# Revit family: ON5DMXA-NRG
name_source: partatom
category: Mechanical Equipment
units: mm (PartAtom-declared; Revit-internal decimal feet)

## family parameters
Always vertical = Yes
Cut with Voids When Loaded = No
OmniClass Number = 23.40.40.11.17
OmniClass Title = Refrigerated Cases
Part Type = Normal
Room Calculation Point = No
Round Connector Dimension = Use Radius
Shared = No
Work Plane-Based = Yes

## types (2) — shared parameters
16" Shelf = Yes
18" Shelf = Yes
BOTTOM ELECTRICAL = Yes
BOTTOM REFRIGERATION PIPING = Yes
Certifications = NSF 7, UL471, CSA
DATE = 03/14/2017
DESIGNERS NAME = SHIDDRAMESH
DRAIN LINE = 48"
DRAIN PIPING = Yes
Default Elevation = 48"
Defrosts Per Day = 6
Description = Narrow Self-Contained Multi-Deck Merchandiser
Discharge Air (°F) = 31 °F
Discharge Air Velocity (FPM) = 200 FPM
Drain Pump Amps = 1 A
Drain Pump Watts = 47 W
EQUIPMENT DESCRIPTION = Narrow Self-Contained Multi-Deck Merchandiser
EQUIPMENT MARK = ON5DMXA-NRG
Evaporator (°F) = 0 °F
Evaporator Pan Heater  Amps = 7 A
Evaporator Pan Heater  Watts = 1500 W
Frequency (Hz) = 60 Hz
GLASS = Glass
Height = 81 1/2"
High Efficiency Amps = 0 A
High Efficiency Fan Amps = 0 A
High Efficiency Fan Watts = 28 W
High Efficiency Watts = 28 W
High Power (Cornice) Amps = 0 A
High Power (Cornice) Watts = 0 W
Item Description = Narrow Self-Contained Multi-Deck Merchandiser
LF STD END = Yes
Legend Number = ON5DMXA-NRG
Light Length = 0
Manufacturer = HILL PHOENIX
Maximum Lights Amps = 1 A
Maximum Overcurrent Protection = 35 A
Minimum Circuit Ampacity = 25 A
Model = ON5DMXA-NRG
Number of Fans = 2
PAINTED METAL UPPER SHELF = PAINTED SHELVES
PHASE = 1
REAR REFRIGERATION PIPING = Yes
REF = 28 5/8"
REFRIGERATION PIPING = COPPER PIPE
RT STD END = Yes
Refgn = 8 3/4"
Refrigerant = R404A
STAINLESS STEEL = GALVANIZED STEEL
Standard Power Amps = 0 A
Standard Power Watts = 0 W
Suction Pressure @ Case Outlet (psig) = 58
TOP ELECTRICAL = Yes
TOP REFRIGERATION PIPING = Yes
Timed-Off Defrost Fail-Safe (Min) = 42 (Min)
Timed-Off Defrost Termination Temp = 42 °F
URL = http://www.hillphoenix.com
Volts = 208 V
Width = 35 3/4"
Wire = 3 wire + ground
zero-valued in all types: BTUH Conventional, BTUH Parallel, Lights Per Row

## per-type parameters (varying)
| type | CENTER LINE | Horsepower | Lbs. Of Refrigerant | Length | Length of Cases | Locked Rotor Amps (LRA) (Amps) | Maximum Lights Watts | Running Load Amps (RLA) (Amps) | Timed-Off Defrost Fail Safe (Min) |
| 08' | 48" | 2 | 5.60 | 96" | 96" | 56 A | 144 W | 12 A | -460 °F |
| 06' | 36" | 1-3/4 | 5 | 72" | 72" | 55 A | 100 W | 13 A | 45 °F |

## geometry (parser evidence)
native form markers: Blend x9, Sweep x2
no freeform markers — native parametric forms only
